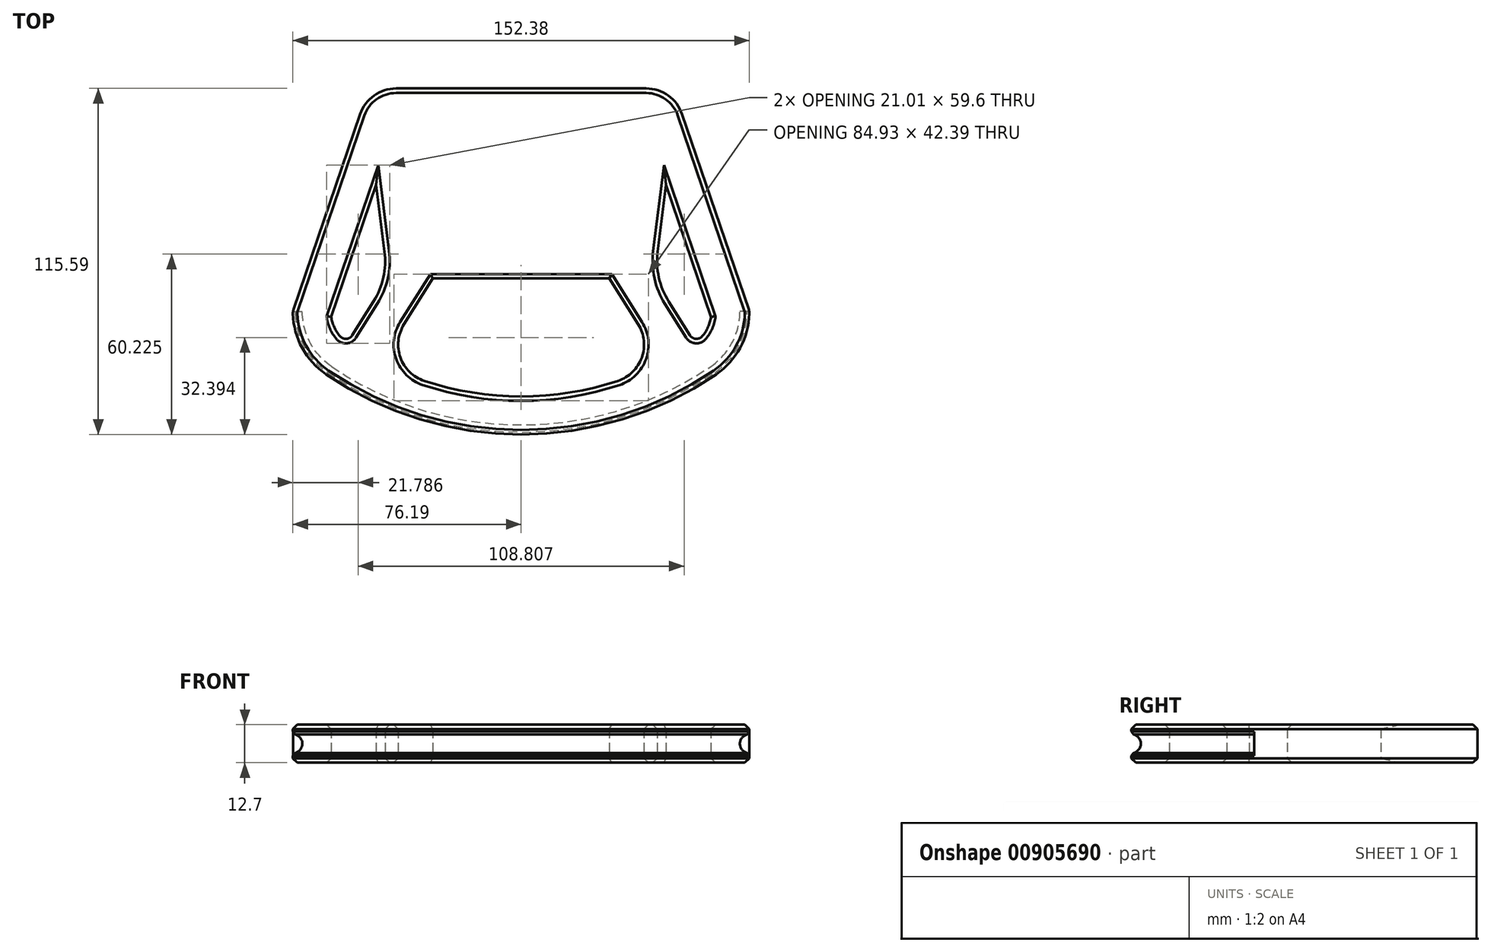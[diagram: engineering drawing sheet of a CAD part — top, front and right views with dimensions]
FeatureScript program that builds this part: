
annotation { "Feature Type Name" : "Feature", "Feature Type Description" : "" }
export const myFeature = defineFeature(function(context is Context, id is Id, definition is map)
    precondition{}
    {
        {
            var Q0;
            Q0=qCreatedBy(makeId("Top.planeOp"),FACE);
            var sketch = newSketch(context, id + "F0", { "sketchPlane" : qUnion([Q0])});
            skLineSegment(sketch, "E0", {"start": v(-76.2, 0) * mm, "end": v(76.2, 0) * mm, "construction": true});
            skPoint(sketch, "E1", {"position": v(0, 0) * mm});
            skArc(sketch, "E2", {"start": v(-65.1, -8.6) * mm, "mid": v(0, -28.67) * mm, "end": v(65.1, -8.6) * mm});
            skLineSegment(sketch, "E3", {"start": v(0, -28.67) * mm, "end": v(0, 85.63) * mm, "construction": true});
            skLineSegment(sketch, "E4", {"start": v(-76.2, 12.4) * mm, "end": v(-76.2, 61.52) * mm, "construction": true});
            skLineSegment(sketch, "E5", {"start": v(-41.71, 86.92) * mm, "end": v(50.8, 86.92) * mm});
            skLineSegment(sketch, "E6", {"start": v(76.2, 61.52) * mm, "end": v(76.2, 12.4) * mm, "construction": true});
            skPoint(sketch, "E7.visualSharp", {"position": v(-76.2, 86.92) * mm});
            skArc(sketch, "E7.filletArc", {"start": v(-50.8, 86.92) * mm, "mid": v(-68.76, 79.48) * mm, "end": v(-76.2, 61.52) * mm, "construction": true});
            skPoint(sketch, "E8.visualSharp", {"position": v(76.2, 86.92) * mm});
            skArc(sketch, "E8.filletArc", {"start": v(76.2, 61.52) * mm, "mid": v(68.76, 79.48) * mm, "end": v(50.8, 86.92) * mm, "construction": true});
            skPoint(sketch, "E9.visualSharp", {"position": v(-76.2, 0) * mm});
            skArc(sketch, "E9.filletArc", {"start": v(-76.2, 12.4) * mm, "mid": v(-73.26, 0.53) * mm, "end": v(-65.1, -8.6) * mm});
            skPoint(sketch, "E10.visualSharp", {"position": v(76.2, 0) * mm});
            skArc(sketch, "E10.filletArc", {"start": v(65.1, -8.6) * mm, "mid": v(73.26, 0.53) * mm, "end": v(76.2, 12.4) * mm, "construction": true});
            skArc(sketch, "E11.0", {"start": v(-63.38, 10.65) * mm, "mid": v(-62.38, 7.18) * mm, "end": v(-60.44, 4.13) * mm});
            skLineSegment(sketch, "E11.1", {"start": v(-63.5, 12.4) * mm, "end": v(-63.5, 61.52) * mm, "construction": true});
            skArc(sketch, "E11.2", {"start": v(-57.95, 1.9) * mm, "mid": v(-56.51, 0.94) * mm, "end": v(-55.06, 0) * mm});
            skArc(sketch, "E11.3", {"start": v(-50.8, 74.22) * mm, "mid": v(-59.78, 70.5) * mm, "end": v(-63.5, 61.52) * mm, "construction": true});
            skArc(sketch, "E11.4", {"start": v(57.95, 1.9) * mm, "mid": v(62.03, 6.46) * mm, "end": v(63.5, 12.4) * mm, "construction": true});
            skLineSegment(sketch, "E11.5", {"start": v(63.5, 61.52) * mm, "end": v(63.5, 12.4) * mm, "construction": true});
            skArc(sketch, "E11.6", {"start": v(63.5, 61.52) * mm, "mid": v(59.78, 70.5) * mm, "end": v(50.8, 74.22) * mm, "construction": true});
            skLineSegment(sketch, "E11.7", {"start": v(-50.8, 74.22) * mm, "end": v(50.8, 74.22) * mm});
            skLineSegment(sketch, "E12", {"start": v(0, 74.22) * mm, "end": v(0, 23.42) * mm, "construction": true});
            skLineSegment(sketch, "E13", {"start": v(-44.45, 23.42) * mm, "end": v(44.45, 23.42) * mm});
            skPoint(sketch, "E14", {"position": v(0, 23.42) * mm});
            skLineSegment(sketch, "E15", {"start": v(-45.57, 32.4) * mm, "end": v(-48.36, 54.7) * mm});
            skLineSegment(sketch, "E16", {"start": v(45.57, 32.4) * mm, "end": v(50.8, 74.22) * mm, "construction": true});
            skLineSegment(sketch, "E17", {"start": v(-49.26, 15.75) * mm, "end": v(-56.36, 4.43) * mm});
            skLineSegment(sketch, "E18", {"start": v(49.26, 15.75) * mm, "end": v(57.95, 1.9) * mm, "construction": true});
            skLineSegment(sketch, "E19.0", {"start": v(-33.7, 16.67) * mm, "end": v(-39.1, 8.05) * mm});
            skLineSegment(sketch, "E20.0", {"start": v(33.7, 16.67) * mm, "end": v(47.2, -4.85) * mm, "construction": true});
            skLineSegment(sketch, "E21", {"start": v(-33.7, 16.67) * mm, "end": v(-29.46, 23.42) * mm});
            skLineSegment(sketch, "E22", {"start": v(33.7, 16.67) * mm, "end": v(29.46, 23.42) * mm, "construction": true});
            skPoint(sketch, "E23.visualSharp", {"position": v(-44.45, 23.42) * mm});
            skArc(sketch, "E23.filletArc", {"start": v(-49.26, 15.75) * mm, "mid": v(-45.98, 23.76) * mm, "end": v(-45.57, 32.4) * mm});
            skPoint(sketch, "E24.visualSharp", {"position": v(44.45, 23.42) * mm});
            skArc(sketch, "E24.filletArc", {"start": v(45.57, 32.4) * mm, "mid": v(45.98, 23.76) * mm, "end": v(49.26, 15.75) * mm, "construction": true});
            skLineSegment(sketch, "E25", {"start": v(-53.73, 78.32) * mm, "end": v(-76.2, 12.4) * mm});
            skPoint(sketch, "E26.visualSharp", {"position": v(-50.8, 86.92) * mm});
            skArc(sketch, "E26.filletArc", {"start": v(-41.71, 86.92) * mm, "mid": v(-49.1, 84.55) * mm, "end": v(-53.73, 78.32) * mm});
            skLineSegment(sketch, "E27.0", {"start": v(-48.36, 54.7) * mm, "end": v(-63.38, 10.65) * mm});
            skArc(sketch, "E28.trimOffspring", {"start": v(-32.34, -10.76) * mm, "mid": v(7.97, -15.66) * mm, "end": v(47.03, -4.6) * mm});
            skArc(sketch, "E29.trimOffspring", {"start": v(55.06, 0) * mm, "mid": v(56.51, 0.94) * mm, "end": v(57.95, 1.9) * mm, "construction": true});
            skPoint(sketch, "E30.visualSharp", {"position": v(-57.95, 1.9) * mm});
            skArc(sketch, "E30.filletArc", {"start": v(-60.44, 4.13) * mm, "mid": v(-58.33, 3.25) * mm, "end": v(-56.36, 4.43) * mm});
            skArc(sketch, "E31.filletArc", {"start": v(-39.1, 8.05) * mm, "mid": v(-40.3, -3) * mm, "end": v(-32.34, -10.76) * mm});
            skArc(sketch, "E32.MirrorCS", {"start": v(39.1, 8.05) * mm, "mid": v(40.3, -3) * mm, "end": v(32.34, -10.76) * mm});
            skLineSegment(sketch, "E33.MirrorCS", {"start": v(33.7, 16.67) * mm, "end": v(39.1, 8.05) * mm});
            skLineSegment(sketch, "E34.MirrorCS", {"start": v(33.7, 16.67) * mm, "end": v(29.46, 23.42) * mm});
            skLineSegment(sketch, "E35.MirrorCS", {"start": v(49.26, 15.75) * mm, "end": v(56.36, 4.43) * mm});
            skArc(sketch, "E36.MirrorCS", {"start": v(60.44, 4.13) * mm, "mid": v(58.33, 3.25) * mm, "end": v(56.36, 4.43) * mm});
            skArc(sketch, "E37.MirrorCS", {"start": v(63.38, 10.65) * mm, "mid": v(62.38, 7.18) * mm, "end": v(60.44, 4.13) * mm});
            skLineSegment(sketch, "E38.MirrorCS", {"start": v(48.36, 54.7) * mm, "end": v(63.38, 10.65) * mm});
            skLineSegment(sketch, "E39.MirrorCS", {"start": v(45.57, 32.4) * mm, "end": v(48.36, 54.7) * mm});
            skArc(sketch, "E40.MirrorCS", {"start": v(49.26, 15.75) * mm, "mid": v(45.98, 23.76) * mm, "end": v(45.57, 32.4) * mm});
            skLineSegment(sketch, "E41.MirrorCS", {"start": v(53.73, 78.32) * mm, "end": v(76.2, 12.4) * mm});
            skArc(sketch, "E42.MirrorCS", {"start": v(76.2, 12.4) * mm, "mid": v(73.26, 0.53) * mm, "end": v(65.1, -8.6) * mm});
            skArc(sketch, "E43.MirrorCS", {"start": v(41.71, 86.92) * mm, "mid": v(49.1, 84.55) * mm, "end": v(53.73, 78.32) * mm});
            skLineSegment(sketch, "E44", {"start": v(-76.2, 12.4) * mm, "end": v(76.2, 12.4) * mm});
            skSolve(sketch);
        }
        {
            var Q0;
            Q0=sQuery(id+"F0.wireOp",EDGE,"E44");
            extrude(context, id + "F1", {"bodyType" : ToolBodyType.SURFACE, "surfaceEntities" : qUnion([Q0]), "depth" : 25.4 * mm, "offsetDistance" : 25.4 * mm});
        }
        {
            var Q0;
            Q0=makeQuery(id+"F0.imprint","IMPRINT",FACE,{"disambiguationData":[TD([[makeQuery(id+"F0.imprint","IMPRINT",EDGE,{"derivedFrom":sQuery(id+"F0.wireOp",EDGE,"E2")}),1.0]])]});
            var Q1;
            {var subQ1=sQuery(id+"F0.wireOp",EDGE,"E15");Q1=makeQuery(id+"F0.imprint","IMPRINT",FACE,{"disambiguationData":[TD([[makeQuery(id+"F0.imprint","IMPRINT",EDGE,{"derivedFrom":subQ1}),-1.0]])]});}
            extrude(context, id + "F2", {"entities" : qUnion([Q0, Q1]), "depth" : 6.35 * mm, "offsetDistance" : 25.4 * mm});
        }
        {
            var Q0;
            Q0=makeQuery(id+"F0.imprint","IMPRINT",FACE,{"disambiguationData":[TD([[makeQuery(id+"F0.imprint","IMPRINT",EDGE,{"derivedFrom":sQuery(id+"F0.wireOp",EDGE,"E2")}),1.0]])]});
            var Q1;
            {var subQ1=sQuery(id+"F0.wireOp",EDGE,"E15");Q1=makeQuery(id+"F0.imprint","IMPRINT",FACE,{"disambiguationData":[TD([[makeQuery(id+"F0.imprint","IMPRINT",EDGE,{"derivedFrom":subQ1}),-1.0]])]});}
            extrude(context, id + "F3", {"entities" : qUnion([Q0, Q1]), "operationType" : NewBodyOperationType.ADD, "oppositeDirection" : true, "depth" : 6.35 * mm, "offsetDistance" : 25.4 * mm});
        }
        {
            var Q0;
            Q0=makeQuery(id+"F1.opExtrude","SWEPT_FACE",FACE,{"disambiguationData":[OSD([sQuery(id+"F0.wireOp",EDGE,"E44")])]});
            var sketch = newSketch(context, id + "F4", { "sketchPlane" : qUnion([Q0])});
            skLineSegment(sketch, "E45", {"start": v(76.2, 0) * mm, "end": v(-76.2, 0) * mm, "construction": true});
            skPoint(sketch, "E46", {"position": v(0, 0) * mm});
            skCircle(sketch, "E47", {"center": v(-76.2, 0) * mm, "radius": 3.18 * mm});
            skSolve(sketch);
        }
        {
            var Q0;
            Q0=makeQuery(id+"F4.imprint","IMPRINT",FACE,{"disambiguationData":[TD([[makeQuery(id+"F4.imprint","IMPRINT",EDGE,{"derivedFrom":sQuery(id+"F4.wireOp",EDGE,"E47")}),1.0]])]});
            var Q1;
            Q1=sQuery(id+"F0.wireOp",EDGE,"E9.filletArc");
            var Q2;
            Q2=sQuery(id+"F0.wireOp",EDGE,"E2");
            var Q3;
            Q3=sQuery(id+"F0.wireOp",EDGE,"E42.MirrorCS");
            sweep(context, id + "F5", {"operationType" : NewBodyOperationType.REMOVE, "profiles" : qUnion([Q0]), "path" : qUnion([Q1, Q2, Q3])});
        }
        {
            var Q0;
            {var subQ0=sQuery(id+"F0.wireOp",EDGE,"E41.MirrorCS");var subQ1=sQuery(id+"F0.wireOp",EDGE,"E44");var subQ2=sQuery(id+"F0.wireOp",EDGE,"E42.MirrorCS");Q0=makeQuery(id+"F5.boolean.opBoolean","SPLIT",EDGE,{"disambiguationData":[topologyDisambiguationEdgeConnected([makeQuery(id+"F2.opExtrude","SWEPT_FACE",FACE,{"disambiguationData":[OSD([subQ0])]}),makeQuery(id+"F3.opExtrude","SWEPT_FACE",FACE,{"disambiguationData":[OSD([subQ0])]}),makeQuery(id+"F5.opSweep","CAP_FACE",FACE,{"disambiguationData":[OSD([sQuery(id+"F0.wireOp",VERTEX,"E42.MirrorCS.start"),sQuery(id+"F4.wireOp",EDGE,"E47")])],"isStart":false})])],"derivedFrom":makeQuery(id+"F3.boolean.opBoolean","MERGE",EDGE,{"derivedFrom":[makeQuery(id+"F2.opExtrude","SWEPT_EDGE",EDGE,{"disambiguationData":[OSD([subQ0,subQ2,subQ1])]}),makeQuery(id+"F3.opExtrude","SWEPT_EDGE",EDGE,{"disambiguationData":[OSD([subQ0,subQ2,subQ1])]})]})});}
            var Q1;
            {var subQ0=sQuery(id+"F0.wireOp",EDGE,"E25");var subQ1=sQuery(id+"F0.wireOp",EDGE,"E44");var subQ2=sQuery(id+"F0.wireOp",EDGE,"E9.filletArc");Q1=makeQuery(id+"F5.boolean.opBoolean","SPLIT",EDGE,{"disambiguationData":[topologyDisambiguationEdgeConnected([makeQuery(id+"F2.opExtrude","SWEPT_FACE",FACE,{"disambiguationData":[OSD([subQ0])]}),makeQuery(id+"F3.opExtrude","SWEPT_FACE",FACE,{"disambiguationData":[OSD([subQ0])]}),makeQuery(id+"F5.opSweep","CAP_FACE",FACE,{"disambiguationData":[OSD([sQuery(id+"F0.wireOp",VERTEX,"E9.filletArc.start"),sQuery(id+"F4.wireOp",EDGE,"E47")])],"isStart":true})])],"derivedFrom":makeQuery(id+"F3.boolean.opBoolean","MERGE",EDGE,{"derivedFrom":[makeQuery(id+"F2.opExtrude","SWEPT_EDGE",EDGE,{"disambiguationData":[OSD([subQ2,subQ0,subQ1])]}),makeQuery(id+"F3.opExtrude","SWEPT_EDGE",EDGE,{"disambiguationData":[OSD([subQ2,subQ0,subQ1])]})]})});}
            fillet(context, id + "F6", {"entities" : qUnion([Q0, Q1]), "radius" : 3.8 * mm, "tangentPropagation" : true, "allowEdgeOverflow" : false});
        }
        {
            var Q0;
            Q0=makeQuery(id+"F3.opExtrude","CAP_FACE",FACE,{"disambiguationData":[OSD([sQuery(id+"F0.wireOp",EDGE,"E2"),sQuery(id+"F0.wireOp",EDGE,"E5"),sQuery(id+"F0.wireOp",EDGE,"E9.filletArc"),sQuery(id+"F0.wireOp",EDGE,"E11.0"),sQuery(id+"F0.wireOp",EDGE,"E13"),sQuery(id+"F0.wireOp",EDGE,"E15"),sQuery(id+"F0.wireOp",EDGE,"E17"),sQuery(id+"F0.wireOp",EDGE,"E19.0"),sQuery(id+"F0.wireOp",EDGE,"E21"),sQuery(id+"F0.wireOp",EDGE,"E23.filletArc"),sQuery(id+"F0.wireOp",EDGE,"E25"),sQuery(id+"F0.wireOp",EDGE,"E26.filletArc"),sQuery(id+"F0.wireOp",EDGE,"E27.0"),sQuery(id+"F0.wireOp",EDGE,"E28.trimOffspring"),sQuery(id+"F0.wireOp",EDGE,"E30.filletArc"),sQuery(id+"F0.wireOp",EDGE,"E31.filletArc"),sQuery(id+"F0.wireOp",EDGE,"E32.MirrorCS"),sQuery(id+"F0.wireOp",EDGE,"E33.MirrorCS"),sQuery(id+"F0.wireOp",EDGE,"E34.MirrorCS"),sQuery(id+"F0.wireOp",EDGE,"E35.MirrorCS"),sQuery(id+"F0.wireOp",EDGE,"E36.MirrorCS"),sQuery(id+"F0.wireOp",EDGE,"E37.MirrorCS"),sQuery(id+"F0.wireOp",EDGE,"E38.MirrorCS"),sQuery(id+"F0.wireOp",EDGE,"E39.MirrorCS"),sQuery(id+"F0.wireOp",EDGE,"E40.MirrorCS"),sQuery(id+"F0.wireOp",EDGE,"E41.MirrorCS"),sQuery(id+"F0.wireOp",EDGE,"E42.MirrorCS"),sQuery(id+"F0.wireOp",EDGE,"E43.MirrorCS")])],"isStart":false});
            var Q1;
            Q1=makeQuery(id+"F2.opExtrude","CAP_FACE",FACE,{"disambiguationData":[OSD([sQuery(id+"F0.wireOp",EDGE,"E2"),sQuery(id+"F0.wireOp",EDGE,"E5"),sQuery(id+"F0.wireOp",EDGE,"E9.filletArc"),sQuery(id+"F0.wireOp",EDGE,"E11.0"),sQuery(id+"F0.wireOp",EDGE,"E13"),sQuery(id+"F0.wireOp",EDGE,"E15"),sQuery(id+"F0.wireOp",EDGE,"E17"),sQuery(id+"F0.wireOp",EDGE,"E19.0"),sQuery(id+"F0.wireOp",EDGE,"E21"),sQuery(id+"F0.wireOp",EDGE,"E23.filletArc"),sQuery(id+"F0.wireOp",EDGE,"E25"),sQuery(id+"F0.wireOp",EDGE,"E26.filletArc"),sQuery(id+"F0.wireOp",EDGE,"E27.0"),sQuery(id+"F0.wireOp",EDGE,"E28.trimOffspring"),sQuery(id+"F0.wireOp",EDGE,"E30.filletArc"),sQuery(id+"F0.wireOp",EDGE,"E31.filletArc"),sQuery(id+"F0.wireOp",EDGE,"E32.MirrorCS"),sQuery(id+"F0.wireOp",EDGE,"E33.MirrorCS"),sQuery(id+"F0.wireOp",EDGE,"E34.MirrorCS"),sQuery(id+"F0.wireOp",EDGE,"E35.MirrorCS"),sQuery(id+"F0.wireOp",EDGE,"E36.MirrorCS"),sQuery(id+"F0.wireOp",EDGE,"E37.MirrorCS"),sQuery(id+"F0.wireOp",EDGE,"E38.MirrorCS"),sQuery(id+"F0.wireOp",EDGE,"E39.MirrorCS"),sQuery(id+"F0.wireOp",EDGE,"E40.MirrorCS"),sQuery(id+"F0.wireOp",EDGE,"E41.MirrorCS"),sQuery(id+"F0.wireOp",EDGE,"E42.MirrorCS"),sQuery(id+"F0.wireOp",EDGE,"E43.MirrorCS")])],"isStart":false});
            chamfer(context, id + "F7", {"entities" : qUnion([Q0, Q1]), "width" : 1.5 * mm, "tangentPropagation" : true});
        }
        {
            var Q0;
            {var subQ0=sQuery(id+"F0.wireOp",EDGE,"E2");Q0=makeQuery(id+"F5.boolean.opBoolean","INTERSECT",EDGE,{"disambiguationData":[OD(1.0)],"derivedFrom":[makeQuery(id+"F3.boolean.opBoolean","MERGE",FACE,{"derivedFrom":[makeQuery(id+"F2.opExtrude","SWEPT_FACE",FACE,{"disambiguationData":[OSD([subQ0])]}),makeQuery(id+"F3.opExtrude","SWEPT_FACE",FACE,{"disambiguationData":[OSD([subQ0])]})]}),makeQuery(id+"F5.opSweep","SWEPT_FACE",FACE,{"disambiguationData":[OSD([subQ0,sQuery(id+"F4.wireOp",EDGE,"E47")])]})]});}
            var Q1;
            {var subQ0=sQuery(id+"F0.wireOp",EDGE,"E9.filletArc");Q1=makeQuery(id+"F5.boolean.opBoolean","INTERSECT",EDGE,{"disambiguationData":[OD(1.0)],"derivedFrom":[makeQuery(id+"F3.boolean.opBoolean","MERGE",FACE,{"derivedFrom":[makeQuery(id+"F2.opExtrude","SWEPT_FACE",FACE,{"disambiguationData":[OSD([subQ0])]}),makeQuery(id+"F3.opExtrude","SWEPT_FACE",FACE,{"disambiguationData":[OSD([subQ0])]})]}),makeQuery(id+"F5.opSweep","SWEPT_FACE",FACE,{"disambiguationData":[OSD([subQ0,sQuery(id+"F4.wireOp",EDGE,"E47")])]})]});}
            var Q2;
            {var subQ0=sQuery(id+"F0.wireOp",EDGE,"E9.filletArc");Q2=makeQuery(id+"F5.boolean.opBoolean","INTERSECT",EDGE,{"disambiguationData":[OD(0.0)],"derivedFrom":[makeQuery(id+"F3.boolean.opBoolean","MERGE",FACE,{"derivedFrom":[makeQuery(id+"F2.opExtrude","SWEPT_FACE",FACE,{"disambiguationData":[OSD([subQ0])]}),makeQuery(id+"F3.opExtrude","SWEPT_FACE",FACE,{"disambiguationData":[OSD([subQ0])]})]}),makeQuery(id+"F5.opSweep","SWEPT_FACE",FACE,{"disambiguationData":[OSD([subQ0,sQuery(id+"F4.wireOp",EDGE,"E47")])]})]});}
            chamfer(context, id + "F8", {"entities" : qUnion([Q0, Q1, Q2]), "width" : 1 * mm, "tangentPropagation" : true});
        }
    });
